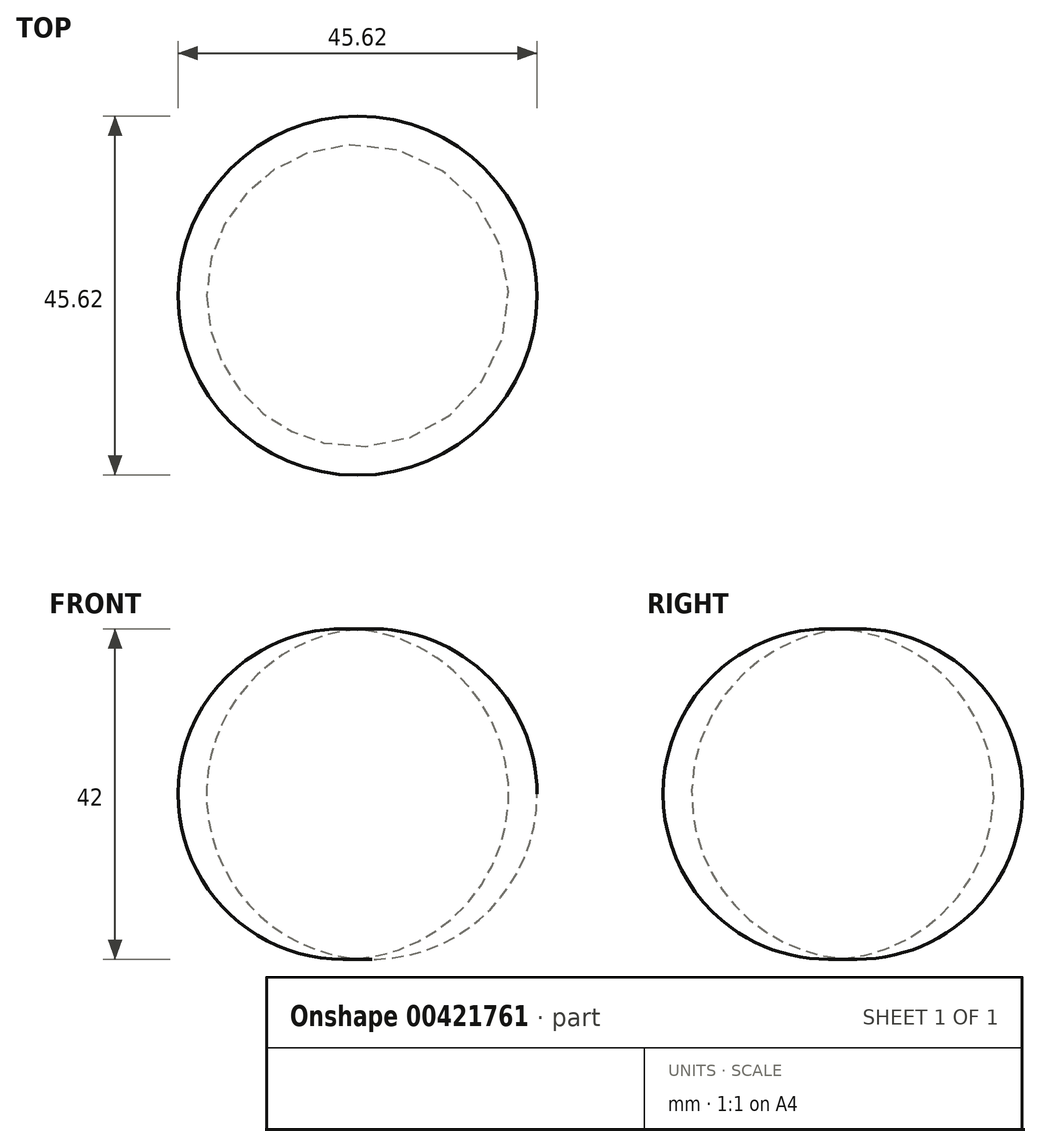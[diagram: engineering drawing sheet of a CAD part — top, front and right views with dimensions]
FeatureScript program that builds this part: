
annotation { "Feature Type Name" : "Feature", "Feature Type Description" : "" }
export const myFeature = defineFeature(function(context is Context, id is Id, definition is map)
    precondition{}
    {
        {
            var Q0;
            Q0=qCreatedBy(makeId("Front.planeOp"),FACE);
            var sketch = newSketch(context, id + "F0", { "sketchPlane" : qUnion([Q0])});
            skArc(sketch, "E0", {"start": v(0, -20.8) * mm, "mid": v(19.19, 0.11) * mm, "end": v(0, 21.03) * mm});
            skLineSegment(sketch, "E1", {"start": v(0, 21.03) * mm, "end": v(0, -20.8) * mm});
            skSolve(sketch);
        }
        {
            var Q0;
            Q0 = qSketchRegion(id + "F0", true);
            var Q1;
            Q1=sQuery(id+"F0.wireOp",EDGE,"E1");
            revolve(context, id + "F1", {"entities" : qUnion([Q0]), "axis" : qUnion([Q1]), "revolveType" : RevolveType.FULL});
        }
    });
